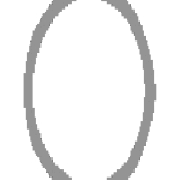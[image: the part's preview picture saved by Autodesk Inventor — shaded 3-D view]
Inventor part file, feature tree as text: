
AUTODESK INVENTOR PART (.ipt)
format: ipt  version: 2021 (Build 250183000, 183)  size: 115,712 bytes
history: native  units: in
note: dims shown in document units (in); Inventor stores cm internally (conversion verified against a paired STEP export)
features: other x4, sketch x3, plane x1
ambient origin geometry x8: Origin, YZ Plane, XZ Plane, XY Plane, X Axis, Y Axis, Z Axis, Center Point
bodies: Solid1 (feature_tree), Body (feature_tree)
feature tree (8):
  other  "Driven Length"
  other  "Frame Generator"
  other  "Start Plane"
  other  "End Plane"
  sketch  "Sketch"  dims[d2=3.5in d4=-0.0in d5=3.5in d6=0.12in d7=0.0in d8=90.0deg d9=3.5in]
  sketch  "Sketch2"  dims[d0=1.0in]
  plane  "Work Plane3"
  sketch  "Sketch3"  dims[d1=0.065in]
